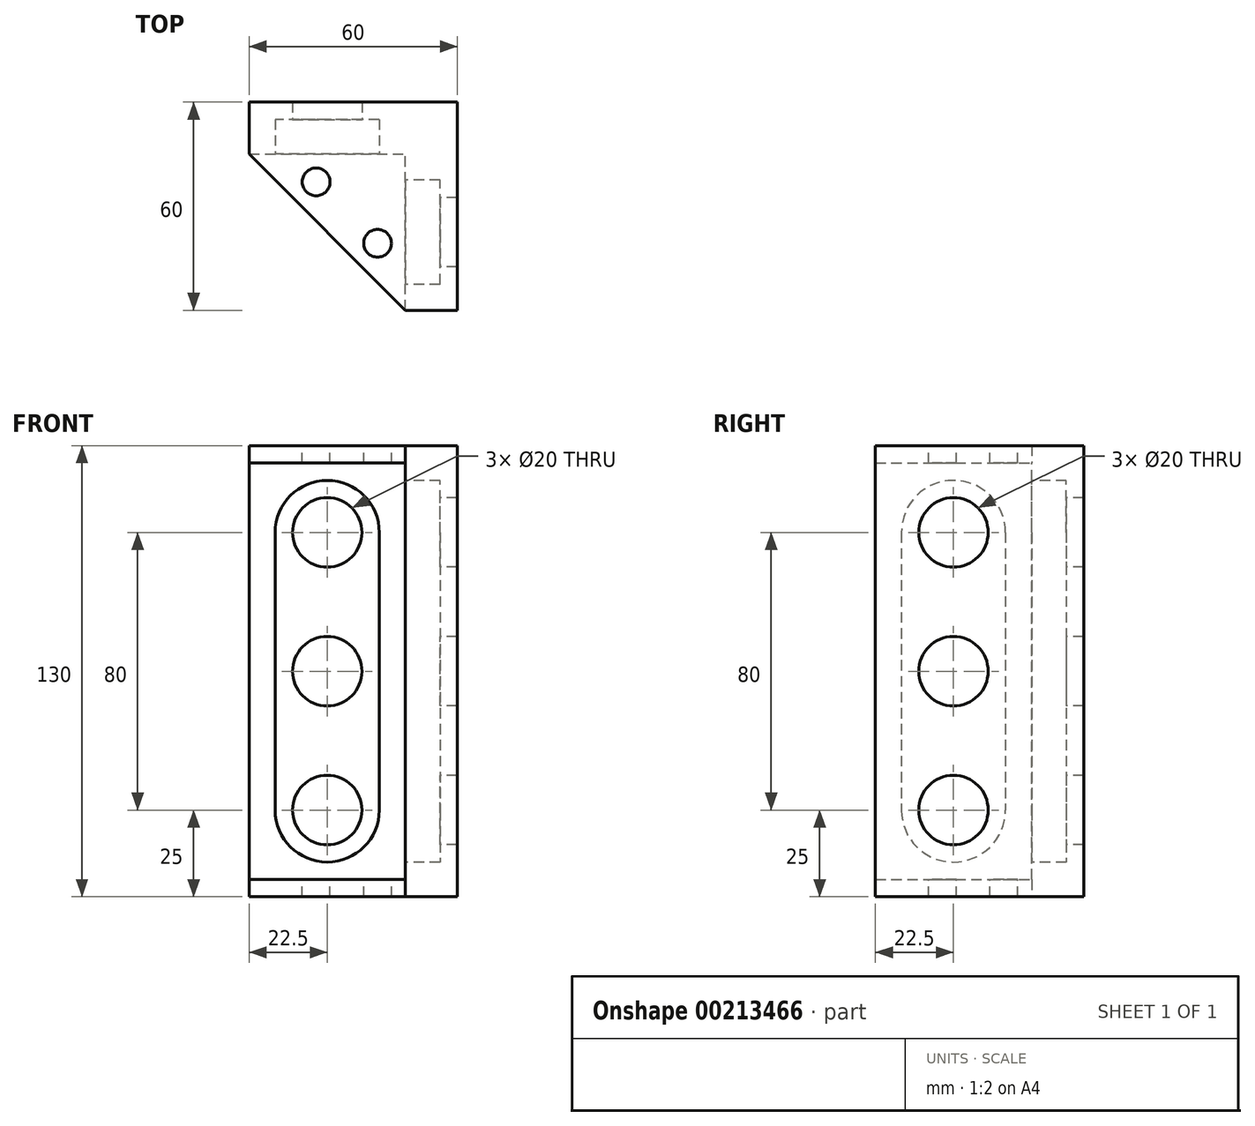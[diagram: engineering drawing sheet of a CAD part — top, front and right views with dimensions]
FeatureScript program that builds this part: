
annotation { "Feature Type Name" : "Feature", "Feature Type Description" : "" }
export const myFeature = defineFeature(function(context is Context, id is Id, definition is map)
    precondition{}
    {
        {
            var Q0;
            Q0=qCreatedBy(makeId("Top.planeOp"),FACE);
            var sketch = newSketch(context, id + "F0", { "sketchPlane" : qUnion([Q0])});
            skLineSegment(sketch, "E0", {"start": v(0, 0) * mm, "end": v(0, 60) * mm});
            skLineSegment(sketch, "E1", {"start": v(0, 60) * mm, "end": v(15, 60) * mm});
            skLineSegment(sketch, "E2", {"start": v(0, 0) * mm, "end": v(60, 0) * mm});
            skLineSegment(sketch, "E3", {"start": v(60, 0) * mm, "end": v(60, 15) * mm});
            skLineSegment(sketch, "E4", {"start": v(60, 15) * mm, "end": v(15, 60) * mm});
            skSolve(sketch);
        }
        {
            var Q0;
            Q0=makeQuery(id+"F0.imprint","IMPRINT",FACE,{"disambiguationData":[TD([[makeQuery(id+"F0.imprint","IMPRINT",EDGE,{"derivedFrom":sQuery(id+"F0.wireOp",EDGE,"E0")}),-1.0]])]});
            extrude(context, id + "F1", {"entities" : qUnion([Q0]), "depth" : 130 * mm});
        }
        {
            var Q0;
            Q0=makeQuery(id+"F1.opExtrude","CAP_FACE",FACE,{"disambiguationData":[OSD([sQuery(id+"F0.wireOp",EDGE,"E0"),sQuery(id+"F0.wireOp",EDGE,"E1"),sQuery(id+"F0.wireOp",EDGE,"E2"),sQuery(id+"F0.wireOp",EDGE,"E3"),sQuery(id+"F0.wireOp",EDGE,"E4")])],"isStart":false});
            var sketch = newSketch(context, id + "F2", { "sketchPlane" : qUnion([Q0])});
            skLineSegment(sketch, "E5", {"start": v(0, 0) * mm, "end": v(37.5, 37.5) * mm, "construction": true});
            skLineSegment(sketch, "E6", {"start": v(60, 15) * mm, "end": v(15, 15) * mm});
            skLineSegment(sketch, "E7", {"start": v(15, 60) * mm, "end": v(15, 15) * mm});
            skLineSegment(sketch, "E8", {"start": v(60, 15) * mm, "end": v(15, 60) * mm});
            skSolve(sketch);
        }
        {
            var Q0;
            Q0=makeQuery(id+"F2.imprint","IMPRINT",FACE,{"disambiguationData":[TD([[makeQuery(id+"F2.imprint","IMPRINT",EDGE,{"derivedFrom":sQuery(id+"F2.wireOp",EDGE,"E6")}),-1.0]])]});
            extrude(context, id + "F3", {"entities" : qUnion([Q0]), "operationType" : NewBodyOperationType.REMOVE, "oppositeDirection" : true, "depth" : 125 * mm});
        }
        {
            var Q0;
            Q0=makeQuery(id+"F3.boolean.opBoolean","COPY",FACE,{"derivedFrom":makeQuery(id+"F3.opExtrude","SWEPT_FACE",FACE,{"disambiguationData":[OSD([sQuery(id+"F2.wireOp",EDGE,"E6")])]})});
            var sketch = newSketch(context, id + "F4", { "sketchPlane" : qUnion([Q0])});
            skLineSegment(sketch, "E9", {"start": v(-37.5, 130) * mm, "end": v(-37.5, 5) * mm, "construction": true});
            skLineSegment(sketch, "E10", {"start": v(-70.35, 105) * mm, "end": v(-9.13, 105) * mm, "construction": true});
            skLineSegment(sketch, "E11", {"start": v(-70.95, 25) * mm, "end": v(10.58, 25) * mm, "construction": true});
            skArc(sketch, "E12", {"start": v(-22.5, 105) * mm, "mid": v(-37.5, 120) * mm, "end": v(-52.5, 105) * mm});
            skArc(sketch, "E13", {"start": v(-52.5, 25) * mm, "mid": v(-37.5, 10) * mm, "end": v(-22.5, 25) * mm});
            skLineSegment(sketch, "E14", {"start": v(-52.5, 105) * mm, "end": v(-52.5, 25) * mm});
            skLineSegment(sketch, "E15", {"start": v(-22.5, 105) * mm, "end": v(-22.5, 25) * mm});
            skSolve(sketch);
        }
        {
            var Q0;
            Q0=makeQuery(id+"F3.boolean.opBoolean","COPY",FACE,{"derivedFrom":makeQuery(id+"F3.opExtrude","SWEPT_FACE",FACE,{"disambiguationData":[OSD([sQuery(id+"F2.wireOp",EDGE,"E7")])]})});
            var sketch = newSketch(context, id + "F5", { "sketchPlane" : qUnion([Q0])});
            skLineSegment(sketch, "E16", {"start": v(37.5, 130) * mm, "end": v(37.5, 5) * mm, "construction": true});
            skLineSegment(sketch, "E17", {"start": v(67.6, 105) * mm, "end": v(3.62, 105) * mm, "construction": true});
            skLineSegment(sketch, "E18", {"start": v(69.99, 25) * mm, "end": v(6.8, 25) * mm, "construction": true});
            skArc(sketch, "E19", {"start": v(52.5, 105) * mm, "mid": v(37.5, 120) * mm, "end": v(22.5, 105) * mm});
            skArc(sketch, "E20", {"start": v(22.5, 25) * mm, "mid": v(37.5, 10) * mm, "end": v(52.5, 25) * mm});
            skLineSegment(sketch, "E21", {"start": v(52.5, 105) * mm, "end": v(52.5, 25) * mm});
            skLineSegment(sketch, "E22", {"start": v(22.5, 105) * mm, "end": v(22.5, 25) * mm});
            skSolve(sketch);
        }
        {
            var Q0;
            Q0=makeQuery(id+"F5.imprint","IMPRINT",FACE,{"disambiguationData":[TD([[makeQuery(id+"F5.imprint","IMPRINT",EDGE,{"derivedFrom":sQuery(id+"F5.wireOp",EDGE,"E19")}),1.0]])]});
            extrude(context, id + "F6", {"entities" : qUnion([Q0]), "operationType" : NewBodyOperationType.REMOVE, "oppositeDirection" : true, "depth" : 10 * mm});
        }
        {
            var Q0;
            Q0=makeQuery(id+"F4.imprint","IMPRINT",FACE,{"disambiguationData":[TD([[makeQuery(id+"F4.imprint","IMPRINT",EDGE,{"derivedFrom":sQuery(id+"F4.wireOp",EDGE,"E12")}),1.0]])]});
            extrude(context, id + "F7", {"entities" : qUnion([Q0]), "operationType" : NewBodyOperationType.REMOVE, "oppositeDirection" : true, "depth" : 10 * mm});
        }
        {
            var Q0;
            Q0=makeQuery(id+"F1.opExtrude","CAP_FACE",FACE,{"disambiguationData":[OSD([sQuery(id+"F0.wireOp",EDGE,"E0"),sQuery(id+"F0.wireOp",EDGE,"E1"),sQuery(id+"F0.wireOp",EDGE,"E2"),sQuery(id+"F0.wireOp",EDGE,"E3"),sQuery(id+"F0.wireOp",EDGE,"E4")])],"isStart":false});
            var sketch = newSketch(context, id + "F8", { "sketchPlane" : qUnion([Q0])});
            skLineSegment(sketch, "E23", {"start": v(60, 15) * mm, "end": v(15, 15) * mm});
            skLineSegment(sketch, "E24", {"start": v(15, 15) * mm, "end": v(15, 60) * mm});
            skLineSegment(sketch, "E25", {"start": v(15, 60) * mm, "end": v(60, 15) * mm});
            skSolve(sketch);
        }
        {
            var Q0;
            Q0=makeQuery(id+"F8.imprint","IMPRINT",FACE,{"disambiguationData":[TD([[makeQuery(id+"F8.imprint","IMPRINT",EDGE,{"derivedFrom":sQuery(id+"F8.wireOp",EDGE,"E23")}),-1.0]])]});
            extrude(context, id + "F9", {"entities" : qUnion([Q0]), "operationType" : NewBodyOperationType.ADD, "oppositeDirection" : true, "depth" : 5 * mm});
        }
        {
            var Q0;
            Q0=makeQuery(id+"F7.boolean.opBoolean","COPY",FACE,{"derivedFrom":makeQuery(id+"F7.opExtrude","CAP_FACE",FACE,{"disambiguationData":[OSD([sQuery(id+"F4.wireOp",EDGE,"E12"),sQuery(id+"F4.wireOp",EDGE,"E13"),sQuery(id+"F4.wireOp",EDGE,"E14"),sQuery(id+"F4.wireOp",EDGE,"E15")])],"isStart":false})});
            var sketch = newSketch(context, id + "F10", { "sketchPlane" : qUnion([Q0])});
            skLineSegment(sketch, "E26", {"start": v(-37.5, 105) * mm, "end": v(-37.5, 25) * mm, "construction": true});
            skCircle(sketch, "E27", {"center": v(-37.5, 105) * mm, "radius": 10 * mm});
            skCircle(sketch, "E28", {"center": v(-37.5, 25) * mm, "radius": 10 * mm});
            skCircle(sketch, "E29", {"center": v(-37.5, 65) * mm, "radius": 5 * mm, "construction": true});
            skCircle(sketch, "E30", {"center": v(-37.5, 65) * mm, "radius": 10 * mm});
            skSolve(sketch);
        }
        {
            var Q0;
            Q0=makeQuery(id+"F10.imprint","IMPRINT",FACE,{"disambiguationData":[TD([[makeQuery(id+"F10.imprint","IMPRINT",EDGE,{"derivedFrom":sQuery(id+"F10.wireOp",EDGE,"E27")}),1.0]])]});
            var Q1;
            Q1=makeQuery(id+"F10.imprint","IMPRINT",FACE,{"disambiguationData":[TD([[makeQuery(id+"F10.imprint","IMPRINT",EDGE,{"derivedFrom":sQuery(id+"F10.wireOp",EDGE,"E30")}),1.0]])]});
            var Q2;
            Q2=makeQuery(id+"F10.imprint","IMPRINT",FACE,{"disambiguationData":[TD([[makeQuery(id+"F10.imprint","IMPRINT",EDGE,{"derivedFrom":sQuery(id+"F10.wireOp",EDGE,"E28")}),1.0]])]});
            extrude(context, id + "F11", {"entities" : qUnion([Q0, Q1, Q2]), "operationType" : NewBodyOperationType.REMOVE, "endBound" : BoundingType.THROUGH_ALL, "oppositeDirection" : true, "depth" : 25 * mm});
        }
        {
            var Q0;
            Q0=makeQuery(id+"F6.boolean.opBoolean","COPY",FACE,{"derivedFrom":makeQuery(id+"F6.opExtrude","CAP_FACE",FACE,{"disambiguationData":[OSD([sQuery(id+"F5.wireOp",EDGE,"E19"),sQuery(id+"F5.wireOp",EDGE,"E20"),sQuery(id+"F5.wireOp",EDGE,"E21"),sQuery(id+"F5.wireOp",EDGE,"E22")])],"isStart":false})});
            var sketch = newSketch(context, id + "F12", { "sketchPlane" : qUnion([Q0])});
            skLineSegment(sketch, "E31", {"start": v(37.5, 105) * mm, "end": v(37.5, 25) * mm, "construction": true});
            skCircle(sketch, "E32", {"center": v(37.5, 105) * mm, "radius": 10 * mm});
            skCircle(sketch, "E33", {"center": v(37.5, 25) * mm, "radius": 10 * mm});
            skCircle(sketch, "E34", {"center": v(37.5, 65) * mm, "radius": 5 * mm, "construction": true});
            skCircle(sketch, "E35", {"center": v(37.5, 65) * mm, "radius": 10 * mm});
            skSolve(sketch);
        }
        {
            var Q0;
            Q0=makeQuery(id+"F12.imprint","IMPRINT",FACE,{"disambiguationData":[TD([[makeQuery(id+"F12.imprint","IMPRINT",EDGE,{"derivedFrom":sQuery(id+"F12.wireOp",EDGE,"E32")}),1.0]])]});
            var Q1;
            Q1=makeQuery(id+"F12.imprint","IMPRINT",FACE,{"disambiguationData":[TD([[makeQuery(id+"F12.imprint","IMPRINT",EDGE,{"derivedFrom":sQuery(id+"F12.wireOp",EDGE,"E35")}),1.0]])]});
            var Q2;
            Q2=makeQuery(id+"F12.imprint","IMPRINT",FACE,{"disambiguationData":[TD([[makeQuery(id+"F12.imprint","IMPRINT",EDGE,{"derivedFrom":sQuery(id+"F12.wireOp",EDGE,"E33")}),1.0]])]});
            extrude(context, id + "F13", {"entities" : qUnion([Q0, Q1, Q2]), "operationType" : NewBodyOperationType.REMOVE, "endBound" : BoundingType.THROUGH_ALL, "oppositeDirection" : true, "depth" : 25 * mm});
        }
        {
            var Q0;
            Q0=makeQuery(id+"F9.boolean.opBoolean","MERGE",FACE,{"derivedFrom":[makeQuery(id+"F1.opExtrude","CAP_FACE",FACE,{"disambiguationData":[OSD([sQuery(id+"F0.wireOp",EDGE,"E0"),sQuery(id+"F0.wireOp",EDGE,"E1"),sQuery(id+"F0.wireOp",EDGE,"E2"),sQuery(id+"F0.wireOp",EDGE,"E3"),sQuery(id+"F0.wireOp",EDGE,"E4")])],"isStart":false}),makeQuery(id+"F9.opExtrude","CAP_FACE",FACE,{"disambiguationData":[OSD([sQuery(id+"F8.wireOp",EDGE,"E23"),sQuery(id+"F8.wireOp",EDGE,"E24"),sQuery(id+"F8.wireOp",EDGE,"E25")])],"isStart":true})]});
            var sketch = newSketch(context, id + "F14", { "sketchPlane" : qUnion([Q0])});
            skLineSegment(sketch, "E36", {"start": v(60, 15) * mm, "end": v(0, 15) * mm, "construction": true});
            skLineSegment(sketch, "E37", {"start": v(15, 60) * mm, "end": v(15, 0) * mm, "construction": true});
            skCircle(sketch, "E38", {"center": v(40.69, 23) * mm, "radius": 4 * mm});
            skLineSegment(sketch, "E39", {"start": v(60, 15) * mm, "end": v(15, 60) * mm, "construction": true});
            skCircle(sketch, "E40", {"center": v(23, 40.69) * mm, "radius": 4 * mm});
            skSolve(sketch);
        }
        {
            var Q0;
            Q0=makeQuery(id+"F14.imprint","IMPRINT",FACE,{"disambiguationData":[TD([[makeQuery(id+"F14.imprint","IMPRINT",EDGE,{"derivedFrom":sQuery(id+"F14.wireOp",EDGE,"E38")}),1.0]])]});
            var Q1;
            Q1=makeQuery(id+"F14.imprint","IMPRINT",FACE,{"disambiguationData":[TD([[makeQuery(id+"F14.imprint","IMPRINT",EDGE,{"derivedFrom":sQuery(id+"F14.wireOp",EDGE,"E40")}),1.0]])]});
            extrude(context, id + "F15", {"entities" : qUnion([Q0, Q1]), "operationType" : NewBodyOperationType.REMOVE, "endBound" : BoundingType.THROUGH_ALL, "oppositeDirection" : true, "depth" : 25 * mm});
        }
        {
            var Q0;
            Q0=makeQuery(id+"F1.opExtrude","SWEPT_BODY",BODY,{"disambiguationData":[OSD([sQuery(id+"F0.wireOp",EDGE,"E0"),sQuery(id+"F0.wireOp",EDGE,"E1"),sQuery(id+"F0.wireOp",EDGE,"E2"),sQuery(id+"F0.wireOp",EDGE,"E3"),sQuery(id+"F0.wireOp",EDGE,"E4")])]});
            var Q1;
            Q1=makeQuery(id+"F1.opExtrude","SWEPT_EDGE",EDGE,{"disambiguationData":[OSD([sQuery(id+"F0.wireOp",EDGE,"E0"),sQuery(id+"F0.wireOp",EDGE,"E2")])]});
            transform(context, id + "F16", {"entities" : qUnion([Q0]), "transformType" : TransformType.ROTATION, "transformAxis" : qUnion([Q1]), "angle" : 180 * degree, "makeCopy" : false});
        }
    });
